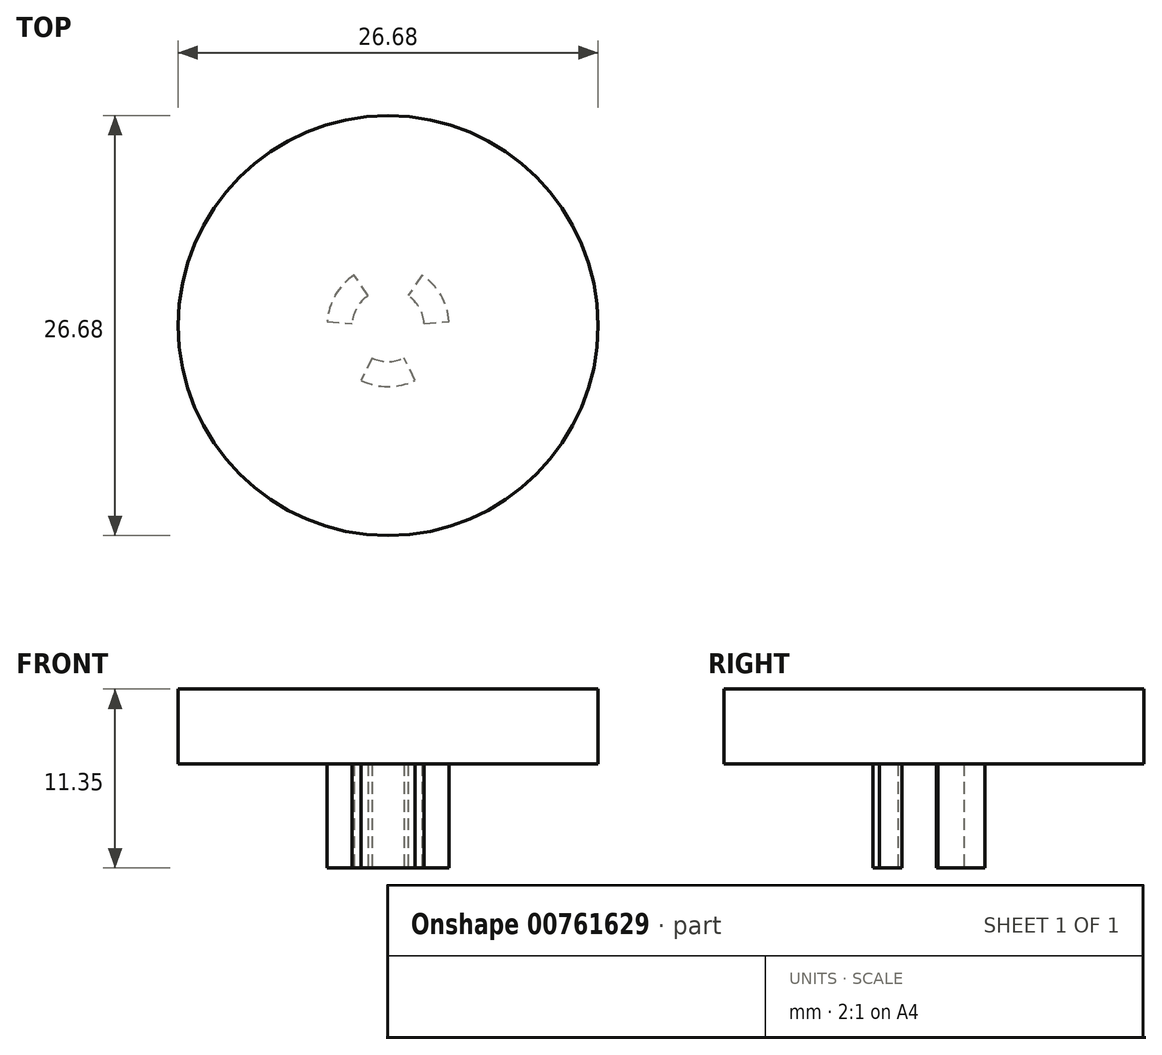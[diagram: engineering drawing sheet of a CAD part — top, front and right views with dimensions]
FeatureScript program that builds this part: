
annotation { "Feature Type Name" : "Feature", "Feature Type Description" : "" }
export const myFeature = defineFeature(function(context is Context, id is Id, definition is map)
    precondition{}
    {
        {
            var Q0;
            Q0=qCreatedBy(makeId("Top.planeOp"),FACE);
            var sketch = newSketch(context, id + "F0", { "sketchPlane" : qUnion([Q0])});
            skCircle(sketch, "E0", {"center": v(0, 0) * mm, "radius": 13.34 * mm});
            skCircle(sketch, "E1", {"center": v(0, 0) * mm, "radius": 3.87 * mm});
            skCircle(sketch, "E2", {"center": v(0, 0) * mm, "radius": 2.03 * mm});
            skLineSegment(sketch, "E3", {"start": v(2.03, 0) * mm, "end": v(3.87, 0) * mm});
            skLineSegment(sketch, "E4", {"start": v(2.03, -0.13) * mm, "end": v(3.87, -0.25) * mm});
            skLineSegment(sketch, "E5", {"start": v(3.87, -0.25) * mm, "end": v(2.03, -0.13) * mm});
            skLineSegment(sketch, "E6", {"start": v(2.03, 0.13) * mm, "end": v(3.87, 0.25) * mm});
            skLineSegment(sketch, "E7.1.0", {"start": v(0.9, 1.82) * mm, "end": v(1.71, 3.47) * mm});
            skLineSegment(sketch, "E7.1.1", {"start": v(2.15, 3.22) * mm, "end": v(1.13, 1.69) * mm});
            skLineSegment(sketch, "E7.2.0", {"start": v(-1.13, 1.69) * mm, "end": v(-2.15, 3.22) * mm});
            skLineSegment(sketch, "E7.2.1", {"start": v(-1.71, 3.47) * mm, "end": v(-0.9, 1.82) * mm});
            skLineSegment(sketch, "E7.3.0", {"start": v(-2.03, -0.13) * mm, "end": v(-3.87, -0.25) * mm});
            skLineSegment(sketch, "E7.3.1", {"start": v(-3.87, 0.25) * mm, "end": v(-2.03, 0.13) * mm});
            skLineSegment(sketch, "E7.4.0", {"start": v(-0.9, -1.82) * mm, "end": v(-1.71, -3.47) * mm});
            skLineSegment(sketch, "E7.4.1", {"start": v(-2.15, -3.22) * mm, "end": v(-1.13, -1.69) * mm});
            skLineSegment(sketch, "E7.5.0", {"start": v(1.13, -1.69) * mm, "end": v(2.15, -3.22) * mm});
            skLineSegment(sketch, "E7.5.1", {"start": v(1.71, -3.47) * mm, "end": v(0.9, -1.82) * mm});
            skSolve(sketch);
        }
        {
            var Q0;
            {var subQ0=sQuery(id+"F0.wireOp",EDGE,"E7.4.0");Q0=makeQuery(id+"F0.imprint","IMPRINT",FACE,{"disambiguationData":[TD([[makeQuery(id+"F0.imprint","IMPRINT",EDGE,{"derivedFrom":subQ0}),1.0]])]});}
            var Q1;
            {var subQ0=sQuery(id+"F0.wireOp",EDGE,"E7.2.0");Q1=makeQuery(id+"F0.imprint","IMPRINT",FACE,{"disambiguationData":[TD([[makeQuery(id+"F0.imprint","IMPRINT",EDGE,{"derivedFrom":subQ0}),1.0]])]});}
            var Q2;
            {var subQ0=sQuery(id+"F0.wireOp",EDGE,"E6");Q2=makeQuery(id+"F0.imprint","IMPRINT",FACE,{"disambiguationData":[TD([[makeQuery(id+"F0.imprint","IMPRINT",EDGE,{"derivedFrom":subQ0}),1.0]])]});}
            var Q3;
            {var subQ0=sQuery(id+"F0.wireOp",EDGE,"E2");var subQ8=makeQuery(id+"F0.imprint","INTERSECT",VERTEX,{"derivedFrom":[subQ0,sQuery(id+"F0.wireOp",EDGE,"E3")]});Q3=makeQuery(id+"F0.imprint","IMPRINT",FACE,{"disambiguationData":[TD([[makeQuery(id+"F0.imprint","IMPRINT",EDGE,{"disambiguationData":[TD([[subQ8,-1.0]])],"derivedFrom":subQ0}),1.0]])]});}
            extrude(context, id + "F1", {"entities" : qUnion([Q0, Q1, Q2, Q3]), "depth" : 6.6 * mm, "offsetDistance" : 25.4 * mm});
        }
        {
            var Q0;
            Q0=makeQuery(id+"F1.opExtrude","CAP_FACE",FACE,{"disambiguationData":[OSD([sQuery(id+"F0.wireOp",EDGE,"E1"),sQuery(id+"F0.wireOp",EDGE,"E2"),sQuery(id+"F0.wireOp",EDGE,"E6"),sQuery(id+"F0.wireOp",EDGE,"E7.1.1"),sQuery(id+"F0.wireOp",EDGE,"E7.2.0"),sQuery(id+"F0.wireOp",EDGE,"E7.3.1"),sQuery(id+"F0.wireOp",EDGE,"E7.4.0"),sQuery(id+"F0.wireOp",EDGE,"E7.5.1")])],"isStart":false});
            var sketch = newSketch(context, id + "F2", { "sketchPlane" : qUnion([Q0])});
            skCircle(sketch, "E8", {"center": v(0, 0) * mm, "radius": 13.33 * mm});
            skSolve(sketch);
        }
        {
            var Q0;
            Q0=qSketchRegion(id+"F2",true);
            extrude(context, id + "F3", {"entities" : qUnion([Q0]), "operationType" : NewBodyOperationType.ADD, "depth" : 4.75 * mm, "offsetDistance" : 25.4 * mm});
        }
        {
            var Q0;
            Q0=makeQuery(id+"F1.opExtrude","CAP_FACE",FACE,{"disambiguationData":[OSD([sQuery(id+"F0.wireOp",EDGE,"E1"),sQuery(id+"F0.wireOp",EDGE,"E2"),sQuery(id+"F0.wireOp",EDGE,"E6"),sQuery(id+"F0.wireOp",EDGE,"E7.1.1"),sQuery(id+"F0.wireOp",EDGE,"E7.2.0"),sQuery(id+"F0.wireOp",EDGE,"E7.3.1"),sQuery(id+"F0.wireOp",EDGE,"E7.4.0"),sQuery(id+"F0.wireOp",EDGE,"E7.5.1")])],"isStart":true});
            var sketch = newSketch(context, id + "F4", { "sketchPlane" : qUnion([Q0])});
            skCircle(sketch, "E9", {"center": v(0, 0) * mm, "radius": 2.29 * mm});
            skSolve(sketch);
        }
        {
            var Q0;
            Q0 = qSketchRegion(id + "F4", true);
            var Q1;
            Q1=makeQuery(id+"F3.opExtrude","CAP_FACE",FACE,{"disambiguationData":[OSD([sQuery(id+"F2.wireOp",EDGE,"E8")])],"isStart":true});
            extrude(context, id + "F5", {"entities" : qUnion([Q0]), "operationType" : NewBodyOperationType.REMOVE, "endBound" : BoundingType.UP_TO_SURFACE, "oppositeDirection" : true, "depth" : 25.4 * mm, "endBoundEntityFace" : qUnion([Q1]), "offsetDistance" : 25.4 * mm});
        }
    });
